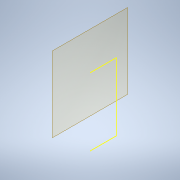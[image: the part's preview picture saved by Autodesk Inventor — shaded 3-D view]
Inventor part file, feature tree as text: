
AUTODESK INVENTOR PART (.ipt)
format: ipt  version: 2020 (Build 240168000, 168)  size: 155,136 bytes
history: native  units: mm
features: reference x5, other x4, sketch x2, plane x1, extrude x1, hole x1, fillet x1
ambient origin geometry x8: Origin, YZ Plane, XZ Plane, XY Plane, X Axis, Y Axis, Z Axis, Center Point
bodies: Solid1 (feature_tree)
feature tree (15):
  plane  "Work Plane1"
  extrude  "Extrusion1"  Depth=19.5mm
  hole  "Hole1"  [1 undecoded]
  fillet  "Fillet1"  Radius=2.0mm
  sketch  "Sketch1"  dims[d0=-15.5mm d1=19.5mm]
  reference  "Reference1"
  reference  "Reference2"
  reference  "Reference3"
  reference  "Reference4"
  reference  "Reference5"
  sketch  "Sketch2"  dims[d2=2.0mm d3=2.0mm d4=2.0mm d5=7.0mm d6=7.0mm d7=2.0mm d8=8.0mm d9=40.8mm d10=15.0mm d11=0.0mm d12=4.5mm d13=9.5mm d14=4.5mm d15=9.5mm d16=48.0mm d17=3.4mm d18=3.4mm d19=2.5mm d20=6.0mm d21=5.0mm d22=2.0mm d23=90.0deg d24=8.0mm d25=20.594885mm d26=2.0mm]
  parser-record x1  (decoder bookkeeping rows leaked as tree rows — omitted from the tree; the rows remain in map.json)
  other  "motorized.iam"
  other  "funnel:1"
  other  "fence:1"
note: 1 required parameter value undecoded (feature->parameter linkage not recoverable at this tier; creation-order binding heuristic only, values carry confidence <= 0.55)
note: 1 file-system path scrubbed to <path> (originals preserved in map.json)
